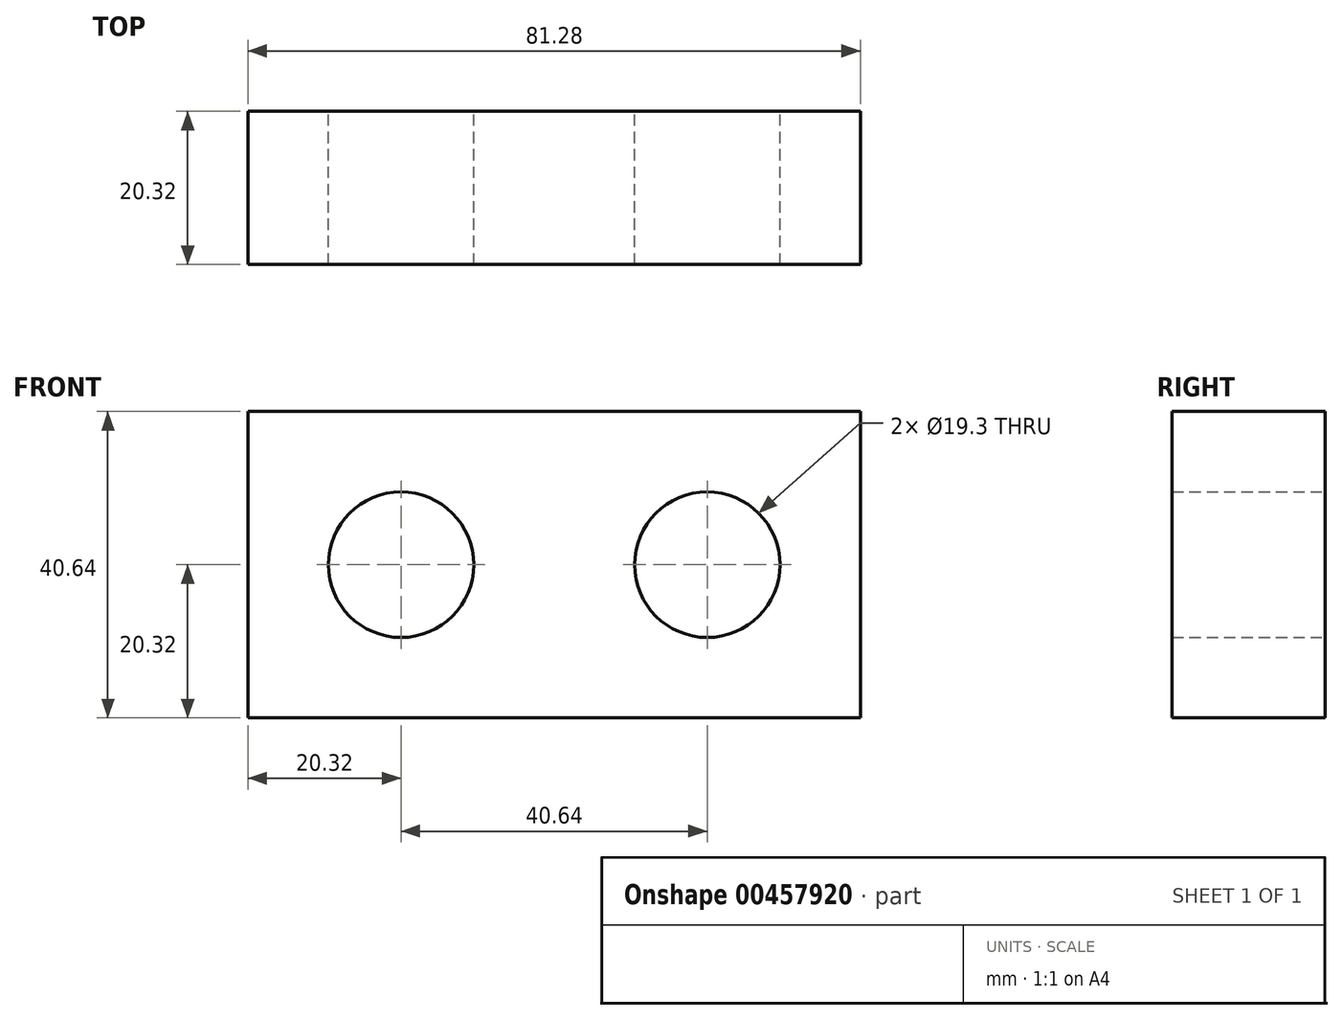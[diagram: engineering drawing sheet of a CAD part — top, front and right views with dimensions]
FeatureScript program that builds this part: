
annotation { "Feature Type Name" : "Feature", "Feature Type Description" : "" }
export const myFeature = defineFeature(function(context is Context, id is Id, definition is map)
    precondition{}
    {
        {
            var Q0;
            Q0=qCreatedBy(makeId("Front.planeOp"),FACE);
            var sketch = newSketch(context, id + "F0", { "sketchPlane" : qUnion([Q0])});
            skLineSegment(sketch, "E0.bottom", {"start": v(0, 40.64) * mm, "end": v(81.28, 40.64) * mm});
            skLineSegment(sketch, "E0.top", {"start": v(0, 0) * mm, "end": v(81.28, 0) * mm});
            skLineSegment(sketch, "E0.left", {"start": v(0, 40.64) * mm, "end": v(0, 0) * mm});
            skLineSegment(sketch, "E0.right", {"start": v(81.28, 40.64) * mm, "end": v(81.28, 0) * mm});
            skLineSegment(sketch, "E1", {"start": v(40.64, 40.64) * mm, "end": v(40.64, 0) * mm, "construction": true});
            skLineSegment(sketch, "E2", {"start": v(40.64, 20.32) * mm, "end": v(0, 20.32) * mm, "construction": true});
            skLineSegment(sketch, "E3", {"start": v(40.64, 20.32) * mm, "end": v(81.28, 20.32) * mm, "construction": true});
            skCircle(sketch, "E4", {"center": v(20.32, 20.32) * mm, "radius": 9.65 * mm});
            skCircle(sketch, "E5", {"center": v(60.96, 20.32) * mm, "radius": 9.65 * mm});
            skSolve(sketch);
        }
        {
            var Q0;
            Q0=makeQuery(id+"F0.imprint","IMPRINT",FACE,{"disambiguationData":[TD([[makeQuery(id+"F0.imprint","IMPRINT",EDGE,{"derivedFrom":sQuery(id+"F0.wireOp",EDGE,"E0.bottom")}),-1.0]])]});
            extrude(context, id + "F1", {"entities" : qUnion([Q0]), "depth" : 20.32 * mm});
        }
    });
